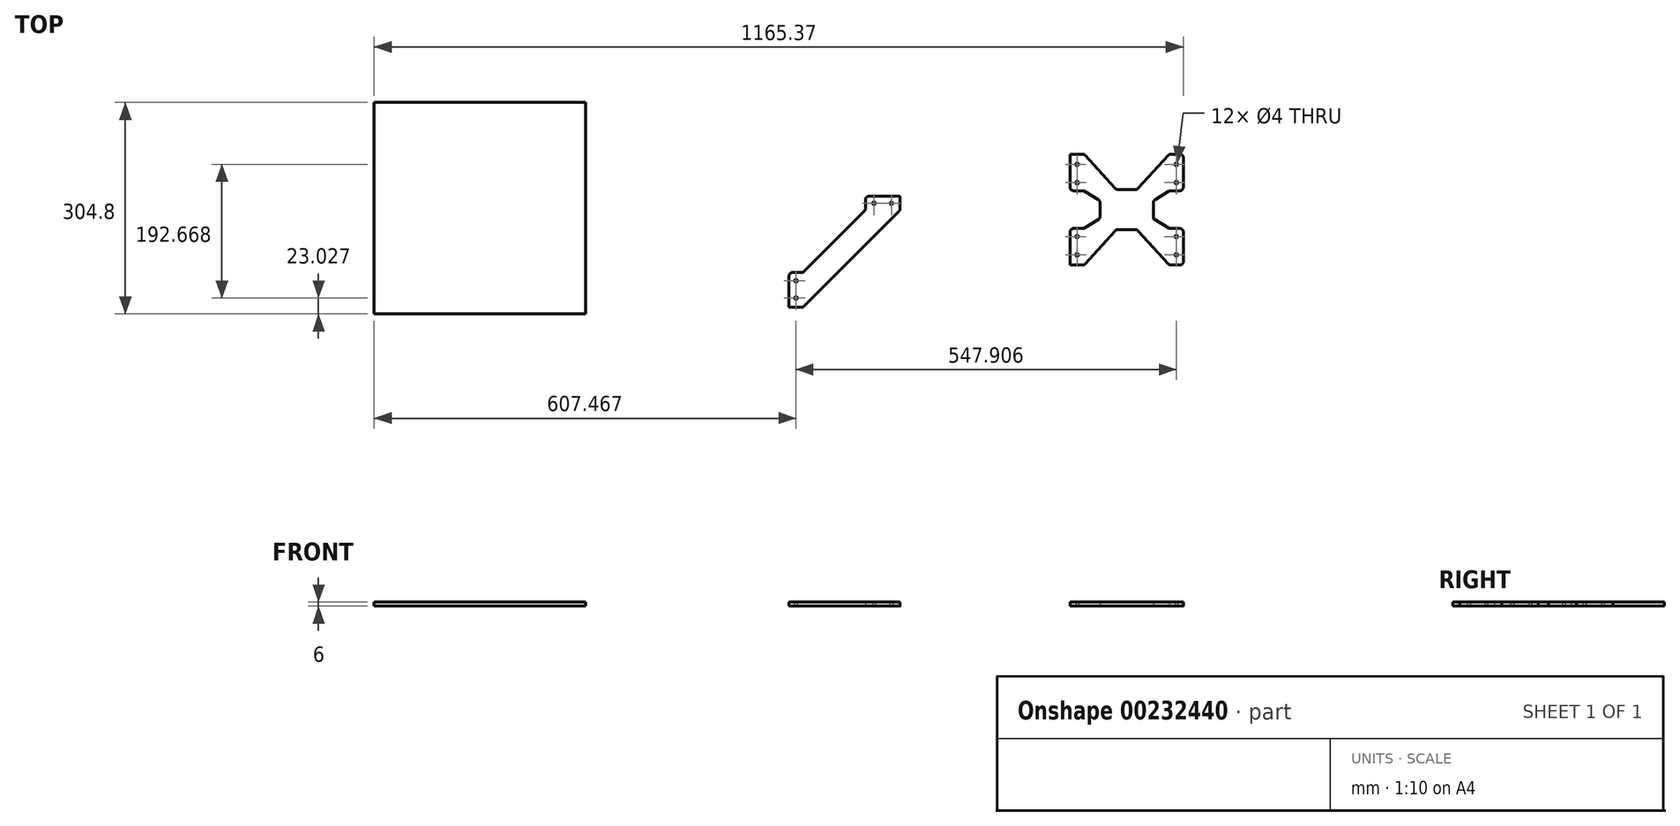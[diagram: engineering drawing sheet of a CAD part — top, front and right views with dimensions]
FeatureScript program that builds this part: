
annotation { "Feature Type Name" : "Feature", "Feature Type Description" : "" }
export const myFeature = defineFeature(function(context is Context, id is Id, definition is map)
    precondition{}
    {
        {
            var Q0;
            Q0=qCreatedBy(makeId("Top.planeOp"),FACE);
            var sketch = newSketch(context, id + "F0", { "sketchPlane" : qUnion([Q0])});
            skLineSegment(sketch, "E0.bottom", {"start": v(0.75, 189.25) * mm, "end": v(163.75, 189.25) * mm, "construction": true});
            skLineSegment(sketch, "E0.top", {"start": v(0.75, 29.25) * mm, "end": v(163.75, 29.25) * mm, "construction": true});
            skLineSegment(sketch, "E0.left", {"start": v(0.75, 189.25) * mm, "end": v(0.75, 136.48) * mm});
            skLineSegment(sketch, "E0.right", {"start": v(163.75, 189.25) * mm, "end": v(163.75, 29.25) * mm, "construction": true});
            skLineSegment(sketch, "E1.bottom", {"start": v(0.75, 189.25) * mm, "end": v(20.75, 189.25) * mm});
            skLineSegment(sketch, "E1.top", {"start": v(0.75, 29.25) * mm, "end": v(20.75, 29.25) * mm});
            skLineSegment(sketch, "E1.left", {"start": v(0.75, 189.25) * mm, "end": v(0.75, 136.48) * mm, "construction": true});
            skLineSegment(sketch, "E1.right", {"start": v(20.75, 136.48) * mm, "end": v(20.75, 82.02) * mm, "construction": true});
            skLineSegment(sketch, "E2", {"start": v(82.25, 189.25) * mm, "end": v(82.25, 29.25) * mm, "construction": true});
            skLineSegment(sketch, "E3", {"start": v(10.75, 189.25) * mm, "end": v(10.75, 29.25) * mm, "construction": true});
            skLineSegment(sketch, "E4", {"start": v(163.75, 109.25) * mm, "end": v(0.75, 109.25) * mm, "construction": true});
            skLineSegment(sketch, "E5.bottom", {"start": v(82.25, 109.25) * mm, "end": v(64.6, 109.25) * mm, "construction": true});
            skLineSegment(sketch, "E5.top", {"start": v(82.25, 138.13) * mm, "end": v(67.25, 138.13) * mm});
            skLineSegment(sketch, "E5.left", {"start": v(82.25, 109.25) * mm, "end": v(82.25, 138.13) * mm, "construction": true});
            skLineSegment(sketch, "E6.bottom", {"start": v(0.75, 189.25) * mm, "end": v(23.8, 189.25) * mm});
            skLineSegment(sketch, "E6.top", {"start": v(0.75, 136.48) * mm, "end": v(20.75, 136.48) * mm});
            skLineSegment(sketch, "E7", {"start": v(20.75, 189.25) * mm, "end": v(67.25, 138.13) * mm});
            skLineSegment(sketch, "E8", {"start": v(20.75, 189.25) * mm, "end": v(0.75, 159.76) * mm, "construction": true});
            skLineSegment(sketch, "E9", {"start": v(0.75, 159.76) * mm, "end": v(20.75, 136.48) * mm, "construction": true});
            skCircle(sketch, "E10", {"center": v(10.75, 174.5) * mm, "radius": 2 * mm});
            skCircle(sketch, "E11", {"center": v(10.75, 148.12) * mm, "radius": 2 * mm});
            skLineSegment(sketch, "E12", {"start": v(20.75, 136.48) * mm, "end": v(43.73, 122.21) * mm});
            skLineSegment(sketch, "E13.MirrorCS", {"start": v(163.75, 189.25) * mm, "end": v(140.7, 189.25) * mm});
            skLineSegment(sketch, "E14.MirrorCS", {"start": v(143.75, 136.48) * mm, "end": v(120.78, 122.21) * mm});
            skLineSegment(sketch, "E15.MirrorCS", {"start": v(163.75, 159.76) * mm, "end": v(143.75, 136.48) * mm, "construction": true});
            skLineSegment(sketch, "E16.MirrorCS", {"start": v(163.75, 136.48) * mm, "end": v(143.75, 136.48) * mm});
            skLineSegment(sketch, "E17.MirrorCS", {"start": v(143.75, 189.25) * mm, "end": v(97.25, 138.13) * mm});
            skLineSegment(sketch, "E18.MirrorCS", {"start": v(163.75, 189.25) * mm, "end": v(163.75, 136.48) * mm});
            skLineSegment(sketch, "E19.MirrorCS", {"start": v(163.75, 189.25) * mm, "end": v(143.75, 189.25) * mm});
            skLineSegment(sketch, "E20.MirrorCS", {"start": v(143.75, 189.25) * mm, "end": v(163.75, 159.76) * mm, "construction": true});
            skCircle(sketch, "E21.MirrorC", {"center": v(153.75, 174.5) * mm, "radius": 2 * mm});
            skCircle(sketch, "E22.MirrorC", {"center": v(153.75, 148.12) * mm, "radius": 2 * mm});
            skLineSegment(sketch, "E23.MirrorCS", {"start": v(82.25, 138.13) * mm, "end": v(97.25, 138.13) * mm});
            skLineSegment(sketch, "E24.MirrorCS", {"start": v(82.25, 109.25) * mm, "end": v(99.9, 109.25) * mm, "construction": true});
            skLineSegment(sketch, "E25.MirrorCS", {"start": v(0.75, 29.25) * mm, "end": v(23.8, 29.25) * mm});
            skLineSegment(sketch, "E26.MirrorCS", {"start": v(163.75, 29.25) * mm, "end": v(143.75, 29.25) * mm});
            skLineSegment(sketch, "E27.MirrorCS", {"start": v(163.75, 29.25) * mm, "end": v(140.7, 29.25) * mm});
            skLineSegment(sketch, "E28.MirrorCS", {"start": v(82.25, 109.25) * mm, "end": v(82.25, 80.37) * mm, "construction": true});
            skLineSegment(sketch, "E29.MirrorCS", {"start": v(143.75, 29.25) * mm, "end": v(163.75, 58.75) * mm, "construction": true});
            skCircle(sketch, "E30.MirrorC", {"center": v(10.75, 44) * mm, "radius": 2 * mm});
            skLineSegment(sketch, "E31.MirrorCS", {"start": v(0.75, 29.25) * mm, "end": v(0.75, 82.02) * mm});
            skLineSegment(sketch, "E32.MirrorCS", {"start": v(163.75, 29.25) * mm, "end": v(163.75, 82.02) * mm});
            skLineSegment(sketch, "E33.MirrorCS", {"start": v(82.25, 80.37) * mm, "end": v(97.25, 80.37) * mm});
            skLineSegment(sketch, "E34.MirrorCS", {"start": v(0.75, 58.75) * mm, "end": v(20.75, 82.02) * mm, "construction": true});
            skLineSegment(sketch, "E35.MirrorCS", {"start": v(20.75, 82.02) * mm, "end": v(43.73, 96.29) * mm});
            skLineSegment(sketch, "E36.MirrorCS", {"start": v(163.75, 82.02) * mm, "end": v(143.75, 82.02) * mm});
            skLineSegment(sketch, "E37.MirrorCS", {"start": v(143.75, 29.25) * mm, "end": v(97.25, 80.37) * mm});
            skCircle(sketch, "E38.MirrorC", {"center": v(153.75, 70.38) * mm, "radius": 2 * mm});
            skCircle(sketch, "E39.MirrorC", {"center": v(153.75, 44) * mm, "radius": 2 * mm});
            skLineSegment(sketch, "E40.MirrorCS", {"start": v(20.75, 29.25) * mm, "end": v(67.25, 80.37) * mm});
            skLineSegment(sketch, "E41.MirrorCS", {"start": v(20.75, 29.25) * mm, "end": v(0.75, 58.75) * mm, "construction": true});
            skLineSegment(sketch, "E42.MirrorCS", {"start": v(82.25, 80.37) * mm, "end": v(67.25, 80.37) * mm});
            skLineSegment(sketch, "E43.MirrorCS", {"start": v(163.75, 58.75) * mm, "end": v(143.75, 82.02) * mm, "construction": true});
            skLineSegment(sketch, "E44.MirrorCS", {"start": v(143.75, 82.02) * mm, "end": v(120.78, 96.29) * mm});
            skLineSegment(sketch, "E45.MirrorCS", {"start": v(0.75, 82.02) * mm, "end": v(20.75, 82.02) * mm});
            skCircle(sketch, "E46.MirrorC", {"center": v(10.75, 70.38) * mm, "radius": 2 * mm});
            skLineSegment(sketch, "E47.trimOffspring", {"start": v(0.75, 82.02) * mm, "end": v(0.75, 29.25) * mm, "construction": true});
            skLineSegment(sketch, "E48.trimOffspring", {"start": v(0.75, 109.25) * mm, "end": v(0.75, 29.25) * mm});
            skLineSegment(sketch, "E49", {"start": v(43.73, 122.21) * mm, "end": v(43.73, 96.29) * mm});
            skLineSegment(sketch, "E50.MirrorCS", {"start": v(120.78, 122.21) * mm, "end": v(120.78, 96.29) * mm});
            skLineSegment(sketch, "E51.top", {"start": v(-404.15, -31.53) * mm, "end": v(-244.15, -31.53) * mm, "construction": true});
            skLineSegment(sketch, "E52.top", {"start": v(-404.15, -31.53) * mm, "end": v(-384.15, -31.53) * mm});
            skLineSegment(sketch, "E52.right", {"start": v(-384.15, 78.47) * mm, "end": v(-384.15, 18.47) * mm, "construction": true});
            skLineSegment(sketch, "E53", {"start": v(-394.15, 128.47) * mm, "end": v(-394.15, -31.53) * mm, "construction": true});
            skLineSegment(sketch, "E54.MirrorCS", {"start": v(-244.15, 128.47) * mm, "end": v(-264.15, 128.47) * mm});
            skLineSegment(sketch, "E55.MirrorCS", {"start": v(-244.15, 128.47) * mm, "end": v(-244.15, 108.47) * mm});
            skLineSegment(sketch, "E56.MirrorCS", {"start": v(-244.15, -31.53) * mm, "end": v(-264.15, -31.53) * mm});
            skCircle(sketch, "E57.MirrorC", {"center": v(-394.15, -18.16) * mm, "radius": 2 * mm});
            skLineSegment(sketch, "E58.MirrorCS", {"start": v(-404.15, -31.53) * mm, "end": v(-404.15, 18.47) * mm});
            skLineSegment(sketch, "E59.MirrorCS", {"start": v(-404.15, -4.8) * mm, "end": v(-384.15, 18.47) * mm, "construction": true});
            skLineSegment(sketch, "E60.MirrorCS", {"start": v(-384.15, -31.53) * mm, "end": v(-404.15, -4.8) * mm, "construction": true});
            skLineSegment(sketch, "E61.MirrorCS", {"start": v(-404.15, 18.47) * mm, "end": v(-384.15, 18.47) * mm});
            skCircle(sketch, "E62.MirrorC", {"center": v(-394.15, 6.84) * mm, "radius": 2 * mm});
            skLineSegment(sketch, "E63.trimOffspring", {"start": v(-404.15, 18.47) * mm, "end": v(-404.15, -31.53) * mm, "construction": true});
            skLineSegment(sketch, "E64.trimOffspring", {"start": v(-404.15, 48.47) * mm, "end": v(-404.15, -31.53) * mm});
            skLineSegment(sketch, "E65.trimOffspring", {"start": v(-375.12, 128.47) * mm, "end": v(-235.12, 128.47) * mm, "construction": true});
            skLineSegment(sketch, "E66.top", {"start": v(-244.15, 128.47) * mm, "end": v(-294.15, 128.47) * mm});
            skLineSegment(sketch, "E66.left", {"start": v(-244.15, 108.47) * mm, "end": v(-244.15, 128.47) * mm});
            skLineSegment(sketch, "E66.right", {"start": v(-294.15, 108.47) * mm, "end": v(-294.15, 128.47) * mm});
            skLineSegment(sketch, "E67", {"start": v(-294.15, 128.47) * mm, "end": v(-269.15, 108.47) * mm, "construction": true});
            skLineSegment(sketch, "E68", {"start": v(-269.15, 108.47) * mm, "end": v(-244.15, 128.47) * mm, "construction": true});
            skCircle(sketch, "E69", {"center": v(-281.65, 118.47) * mm, "radius": 2 * mm});
            skCircle(sketch, "E70", {"center": v(-256.65, 118.47) * mm, "radius": 2 * mm});
            skLineSegment(sketch, "E71", {"start": v(-384.15, 18.47) * mm, "end": v(-294.15, 108.47) * mm});
            skLineSegment(sketch, "E72", {"start": v(-244.15, 108.47) * mm, "end": v(-384.15, -31.53) * mm});
            skLineSegment(sketch, "E73", {"start": v(10.75, 174.5) * mm, "end": v(153.75, 174.5) * mm, "construction": true});
            skSolve(sketch);
        }
        {
            var Q0;
            Q0 = qSketchRegion(id + "F0", true);
            extrude(context, id + "F1", {"entities" : qUnion([Q0]), "depth" : 6 * mm});
        }
        {
            var Q0;
            Q0=makeQuery(id+"F1.opExtrude","SWEPT_EDGE",EDGE,{"disambiguationData":[OSD([sQuery(id+"F0.wireOp",EDGE,"E5.top"),sQuery(id+"F0.wireOp",EDGE,"E7")])]});
            var Q1;
            Q1=makeQuery(id+"F1.opExtrude","SWEPT_EDGE",EDGE,{"disambiguationData":[OSD([sQuery(id+"F0.wireOp",EDGE,"E17.MirrorCS"),sQuery(id+"F0.wireOp",EDGE,"E23.MirrorCS")])]});
            var Q2;
            Q2=makeQuery(id+"F1.opExtrude","SWEPT_EDGE",EDGE,{"disambiguationData":[OSD([sQuery(id+"F0.wireOp",EDGE,"E17.MirrorCS"),sQuery(id+"F0.wireOp",EDGE,"E19.MirrorCS")])]});
            var Q3;
            Q3=makeQuery(id+"F1.opExtrude","SWEPT_EDGE",EDGE,{"disambiguationData":[OSD([sQuery(id+"F0.wireOp",EDGE,"E6.bottom"),sQuery(id+"F0.wireOp",EDGE,"E7")])]});
            var Q4;
            Q4=makeQuery(id+"F1.opExtrude","SWEPT_EDGE",EDGE,{"disambiguationData":[OSD([sQuery(id+"F0.wireOp",EDGE,"E6.top"),sQuery(id+"F0.wireOp",EDGE,"E12")])]});
            var Q5;
            Q5=makeQuery(id+"F1.opExtrude","SWEPT_EDGE",EDGE,{"disambiguationData":[OSD([sQuery(id+"F0.wireOp",EDGE,"E12"),sQuery(id+"F0.wireOp",EDGE,"E49")])]});
            var Q6;
            Q6=makeQuery(id+"F1.opExtrude","SWEPT_EDGE",EDGE,{"disambiguationData":[OSD([sQuery(id+"F0.wireOp",EDGE,"E35.MirrorCS"),sQuery(id+"F0.wireOp",EDGE,"E49")])]});
            var Q7;
            Q7=makeQuery(id+"F1.opExtrude","SWEPT_EDGE",EDGE,{"disambiguationData":[OSD([sQuery(id+"F0.wireOp",EDGE,"E35.MirrorCS"),sQuery(id+"F0.wireOp",EDGE,"E45.MirrorCS")])]});
            var Q8;
            Q8=makeQuery(id+"F1.opExtrude","SWEPT_EDGE",EDGE,{"disambiguationData":[OSD([sQuery(id+"F0.wireOp",EDGE,"E6.bottom"),sQuery(id+"F0.wireOp",EDGE,"E0.left")])]});
            var Q9;
            Q9=makeQuery(id+"F1.opExtrude","SWEPT_EDGE",EDGE,{"disambiguationData":[OSD([sQuery(id+"F0.wireOp",EDGE,"E18.MirrorCS"),sQuery(id+"F0.wireOp",EDGE,"E19.MirrorCS")])]});
            var Q10;
            Q10=makeQuery(id+"F1.opExtrude","SWEPT_EDGE",EDGE,{"disambiguationData":[OSD([sQuery(id+"F0.wireOp",EDGE,"E32.MirrorCS"),sQuery(id+"F0.wireOp",EDGE,"E36.MirrorCS")])]});
            var Q11;
            Q11=makeQuery(id+"F1.opExtrude","SWEPT_EDGE",EDGE,{"disambiguationData":[OSD([sQuery(id+"F0.wireOp",EDGE,"E45.MirrorCS"),sQuery(id+"F0.wireOp",EDGE,"E48.trimOffspring")])]});
            var Q12;
            Q12=makeQuery(id+"F1.opExtrude","SWEPT_EDGE",EDGE,{"disambiguationData":[OSD([sQuery(id+"F0.wireOp",EDGE,"E6.top"),sQuery(id+"F0.wireOp",EDGE,"E0.left")])]});
            var Q13;
            Q13=makeQuery(id+"F1.opExtrude","SWEPT_EDGE",EDGE,{"disambiguationData":[OSD([sQuery(id+"F0.wireOp",EDGE,"E1.top"),sQuery(id+"F0.wireOp",EDGE,"E40.MirrorCS")])]});
            var Q14;
            Q14=makeQuery(id+"F1.opExtrude","SWEPT_EDGE",EDGE,{"disambiguationData":[OSD([sQuery(id+"F0.wireOp",EDGE,"E40.MirrorCS"),sQuery(id+"F0.wireOp",EDGE,"E42.MirrorCS")])]});
            var Q15;
            Q15=makeQuery(id+"F1.opExtrude","SWEPT_EDGE",EDGE,{"disambiguationData":[OSD([sQuery(id+"F0.wireOp",EDGE,"E33.MirrorCS"),sQuery(id+"F0.wireOp",EDGE,"E37.MirrorCS")])]});
            var Q16;
            Q16=makeQuery(id+"F1.opExtrude","SWEPT_EDGE",EDGE,{"disambiguationData":[OSD([sQuery(id+"F0.wireOp",EDGE,"E14.MirrorCS"),sQuery(id+"F0.wireOp",EDGE,"E50.MirrorCS")])]});
            var Q17;
            Q17=makeQuery(id+"F1.opExtrude","SWEPT_EDGE",EDGE,{"disambiguationData":[OSD([sQuery(id+"F0.wireOp",EDGE,"E14.MirrorCS"),sQuery(id+"F0.wireOp",EDGE,"E16.MirrorCS")])]});
            var Q18;
            Q18=makeQuery(id+"F1.opExtrude","SWEPT_EDGE",EDGE,{"disambiguationData":[OSD([sQuery(id+"F0.wireOp",EDGE,"E16.MirrorCS"),sQuery(id+"F0.wireOp",EDGE,"E18.MirrorCS")])]});
            var Q19;
            Q19=makeQuery(id+"F1.opExtrude","SWEPT_EDGE",EDGE,{"disambiguationData":[OSD([sQuery(id+"F0.wireOp",EDGE,"E27.MirrorCS"),sQuery(id+"F0.wireOp",EDGE,"E32.MirrorCS")])]});
            var Q20;
            Q20=makeQuery(id+"F1.opExtrude","SWEPT_EDGE",EDGE,{"disambiguationData":[OSD([sQuery(id+"F0.wireOp",EDGE,"E27.MirrorCS"),sQuery(id+"F0.wireOp",EDGE,"E37.MirrorCS")])]});
            var Q21;
            Q21=makeQuery(id+"F1.opExtrude","SWEPT_EDGE",EDGE,{"disambiguationData":[OSD([sQuery(id+"F0.wireOp",EDGE,"E1.top"),sQuery(id+"F0.wireOp",EDGE,"E48.trimOffspring")])]});
            var Q22;
            Q22=makeQuery(id+"F1.opExtrude","SWEPT_EDGE",EDGE,{"disambiguationData":[OSD([sQuery(id+"F0.wireOp",EDGE,"E66.top"),sQuery(id+"F0.wireOp",EDGE,"E66.right")])]});
            var Q23;
            Q23=makeQuery(id+"F1.opExtrude","SWEPT_EDGE",EDGE,{"disambiguationData":[OSD([sQuery(id+"F0.wireOp",EDGE,"E66.right"),sQuery(id+"F0.wireOp",EDGE,"E71")])]});
            var Q24;
            Q24=makeQuery(id+"F1.opExtrude","SWEPT_EDGE",EDGE,{"disambiguationData":[OSD([sQuery(id+"F0.wireOp",EDGE,"E61.MirrorCS"),sQuery(id+"F0.wireOp",EDGE,"E71")])]});
            var Q25;
            Q25=makeQuery(id+"F1.opExtrude","SWEPT_EDGE",EDGE,{"disambiguationData":[OSD([sQuery(id+"F0.wireOp",EDGE,"E61.MirrorCS"),sQuery(id+"F0.wireOp",EDGE,"E64.trimOffspring")])]});
            var Q26;
            Q26=makeQuery(id+"F1.opExtrude","SWEPT_EDGE",EDGE,{"disambiguationData":[OSD([sQuery(id+"F0.wireOp",EDGE,"E66.top"),sQuery(id+"F0.wireOp",EDGE,"E66.left")])]});
            var Q27;
            Q27=makeQuery(id+"F1.opExtrude","SWEPT_EDGE",EDGE,{"disambiguationData":[OSD([sQuery(id+"F0.wireOp",EDGE,"E66.left"),sQuery(id+"F0.wireOp",EDGE,"E72")])]});
            var Q28;
            Q28=makeQuery(id+"F1.opExtrude","SWEPT_EDGE",EDGE,{"disambiguationData":[OSD([sQuery(id+"F0.wireOp",EDGE,"E52.top"),sQuery(id+"F0.wireOp",EDGE,"E72")])]});
            var Q29;
            Q29=makeQuery(id+"F1.opExtrude","SWEPT_EDGE",EDGE,{"disambiguationData":[OSD([sQuery(id+"F0.wireOp",EDGE,"E52.top"),sQuery(id+"F0.wireOp",EDGE,"E64.trimOffspring")])]});
            fillet(context, id + "F2", {"entities" : qUnion([Q0, Q1, Q2, Q3, Q4, Q5, Q6, Q7, Q8, Q9, Q10, Q11, Q12, Q13, Q14, Q15, Q16, Q17, Q18, Q19, Q20, Q21, Q22, Q23, Q24, Q25, Q26, Q27, Q28, Q29]), "radius" : 5 * mm, "tangentPropagation" : true, "allowEdgeOverflow" : false});
        }
        {
            var Q0;
            Q0=qCreatedBy(makeId("Top.planeOp"),FACE);
            var sketch = newSketch(context, id + "F3", { "sketchPlane" : qUnion([Q0])});
            skLineSegment(sketch, "E74.bottom", {"start": v(-1001.62, 263.61) * mm, "end": v(-696.82, 263.61) * mm});
            skLineSegment(sketch, "E74.top", {"start": v(-1001.62, -41.19) * mm, "end": v(-696.82, -41.19) * mm});
            skLineSegment(sketch, "E74.left", {"start": v(-1001.62, 263.61) * mm, "end": v(-1001.62, -41.19) * mm});
            skLineSegment(sketch, "E74.right", {"start": v(-696.82, 263.61) * mm, "end": v(-696.82, -41.19) * mm});
            skSolve(sketch);
        }
        {
            var Q0;
            Q0 = qSketchRegion(id + "F3", true);
            extrude(context, id + "F4", {"entities" : qUnion([Q0]), "depth" : 6 * mm});
        }
    });
